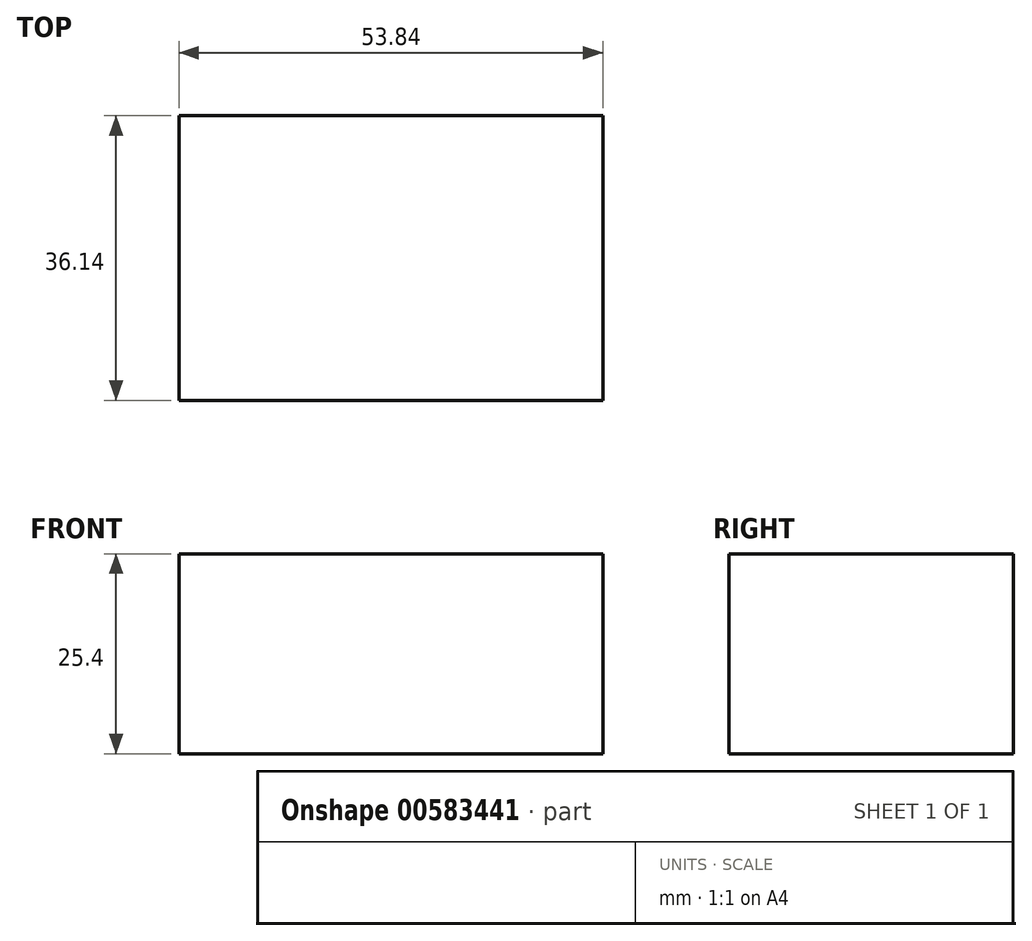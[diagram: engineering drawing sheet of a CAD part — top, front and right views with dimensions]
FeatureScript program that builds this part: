
annotation { "Feature Type Name" : "Feature", "Feature Type Description" : "" }
export const myFeature = defineFeature(function(context is Context, id is Id, definition is map)
    precondition{}
    {
        {
            var Q0;
            Q0=qCreatedBy(makeId("Top.planeOp"),FACE);
            var sketch = newSketch(context, id + "F0", { "sketchPlane" : qUnion([Q0])});
            skLineSegment(sketch, "E0.bottom", {"start": v(0, 13.6) * mm, "end": v(53.84, 13.6) * mm});
            skLineSegment(sketch, "E0.top", {"start": v(0, 49.75) * mm, "end": v(53.84, 49.75) * mm});
            skLineSegment(sketch, "E0.left", {"start": v(0, 13.6) * mm, "end": v(0, 49.75) * mm});
            skLineSegment(sketch, "E0.right", {"start": v(53.84, 13.6) * mm, "end": v(53.84, 49.75) * mm});
            skSolve(sketch);
        }
        {
            var Q0;
            Q0=makeQuery(id+"F0.imprint","IMPRINT",FACE,{"disambiguationData":[TD([[makeQuery(id+"F0.imprint","IMPRINT",EDGE,{"derivedFrom":sQuery(id+"F0.wireOp",EDGE,"E0.bottom")}),1.0]])]});
            extrude(context, id + "F1", {"entities" : qUnion([Q0]), "depth" : 25.4 * mm, "offsetDistance" : 25.4 * mm});
        }
    });
